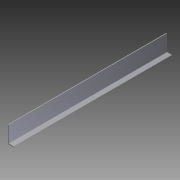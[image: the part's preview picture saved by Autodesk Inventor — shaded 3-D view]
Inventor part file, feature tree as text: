
AUTODESK INVENTOR PART (.ipt)
format: ipt  version: 2012 (Build 160160000, 160)  size: 72,704 bytes
history: native  units: in
note: dims shown in document units (in); Inventor stores cm internally (conversion verified against a paired STEP export)
features: extrude x1, sketch x1
ambient origin geometry x8: Origin, YZ Plane, XZ Plane, XY Plane, X Axis, Y Axis, Z Axis, Center Point
bodies: Solid1 (feature_tree)
feature tree (2):
  extrude  "Extrusion1"  Depth=1.0in
  sketch  "Sketch1"  dims[d0=3.0in d1=1.0in d2=0.125in d3=0.125in d4=28.0in d5=0.0in]
